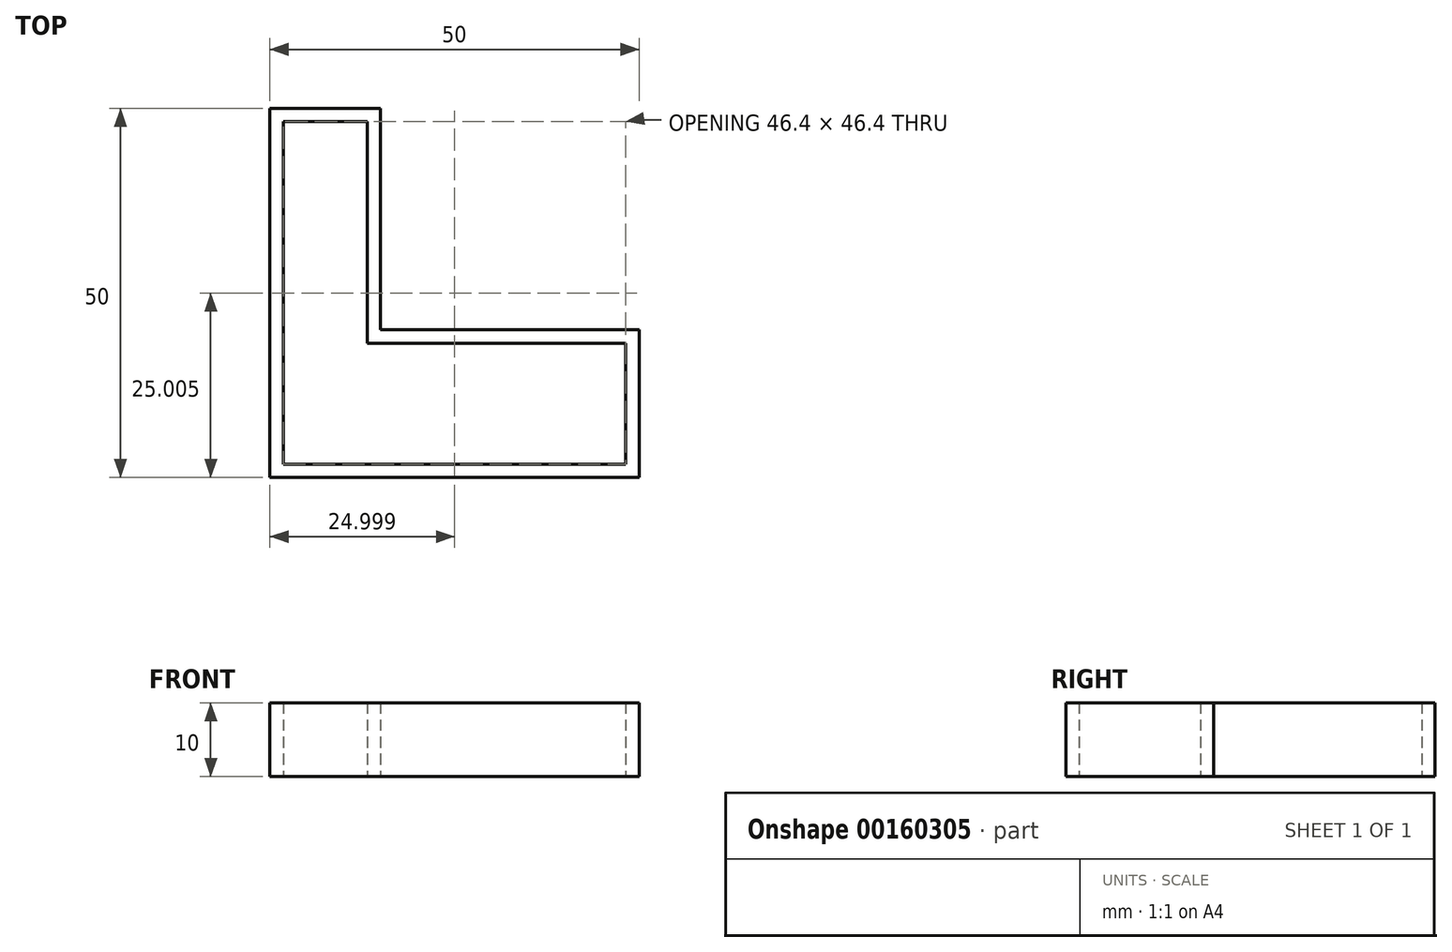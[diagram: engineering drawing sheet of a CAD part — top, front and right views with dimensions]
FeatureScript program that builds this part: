
annotation { "Feature Type Name" : "Feature", "Feature Type Description" : "" }
export const myFeature = defineFeature(function(context is Context, id is Id, definition is map)
    precondition{}
    {
        {
            var Q0;
            Q0=qCreatedBy(makeId("Top.planeOp"),FACE);
            var sketch = newSketch(context, id + "F0", { "sketchPlane" : qUnion([Q0])});
            skLineSegment(sketch, "E0.bottom", {"start": v(-34.08, 35.4) * mm, "end": v(-19.08, 35.4) * mm});
            skLineSegment(sketch, "E0.top", {"start": v(-34.08, -14.6) * mm, "end": v(-19.08, -14.6) * mm});
            skLineSegment(sketch, "E0.left", {"start": v(-34.08, 35.4) * mm, "end": v(-34.08, -14.6) * mm});
            skLineSegment(sketch, "E0.right", {"start": v(-19.08, 35.4) * mm, "end": v(-19.08, -14.6) * mm});
            skLineSegment(sketch, "E1.bottom", {"start": v(-19.08, 5.4) * mm, "end": v(15.92, 5.4) * mm});
            skLineSegment(sketch, "E1.top", {"start": v(-19.08, -14.6) * mm, "end": v(15.92, -14.6) * mm});
            skLineSegment(sketch, "E1.left", {"start": v(-19.08, 5.4) * mm, "end": v(-19.08, -14.6) * mm});
            skLineSegment(sketch, "E1.right", {"start": v(15.92, 5.4) * mm, "end": v(15.92, -14.6) * mm});
            skSolve(sketch);
        }
        {
            var Q0;
            Q0 = qSketchRegion(id + "F0", true);
            extrude(context, id + "F1", {"entities" : qUnion([Q0]), "depth" : 12 * mm});
        }
        {
            var Q0;
            Q0=makeQuery(id+"F1.opExtrude","CAP_FACE",FACE,{"disambiguationData":[OSD([sQuery(id+"F0.wireOp",EDGE,"E0.bottom"),sQuery(id+"F0.wireOp",EDGE,"E0.top"),sQuery(id+"F0.wireOp",EDGE,"E0.left"),sQuery(id+"F0.wireOp",EDGE,"E0.right"),sQuery(id+"F0.wireOp",EDGE,"E1.bottom"),sQuery(id+"F0.wireOp",EDGE,"E1.top"),sQuery(id+"F0.wireOp",EDGE,"E1.right")])],"isStart":false});
            shell(context, id + "F2", {"entities" : qUnion([Q0]), "thickness" : 1.8 * mm});
        }
        {
            var Q0;
            Q0 = qSketchRegion(id + "F0", true);
            extrude(context, id + "F3", {"entities" : qUnion([Q0]), "operationType" : NewBodyOperationType.REMOVE, "depth" : 2 * mm});
        }
    });
